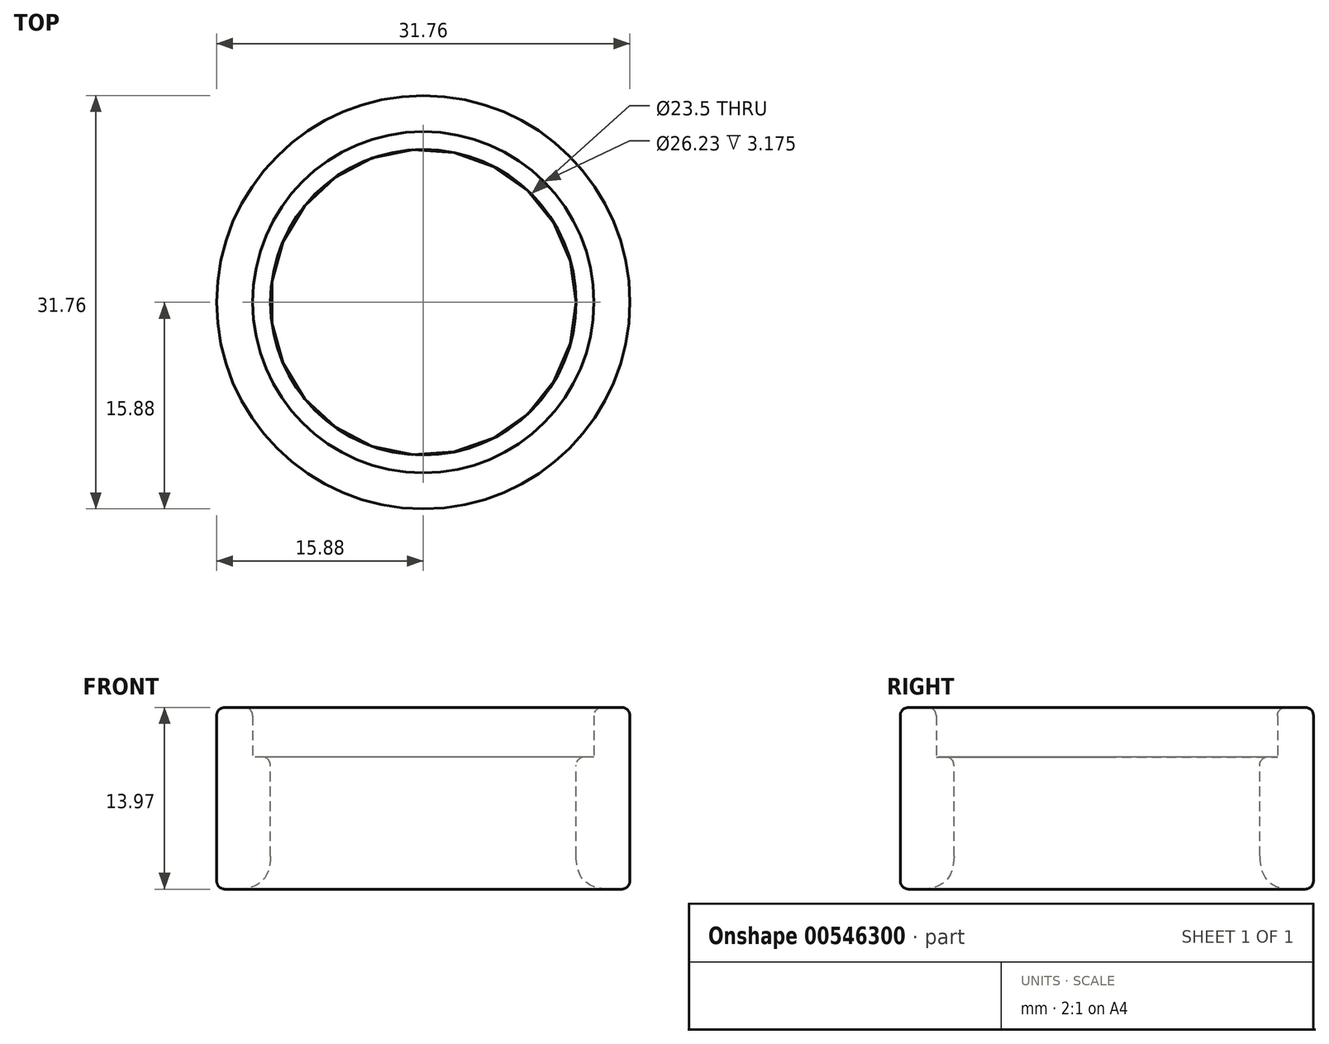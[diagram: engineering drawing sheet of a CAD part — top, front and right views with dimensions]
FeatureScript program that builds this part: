
annotation { "Feature Type Name" : "Feature", "Feature Type Description" : "" }
export const myFeature = defineFeature(function(context is Context, id is Id, definition is map)
    precondition{}
    {
        {
            var Q0;
            Q0=qCreatedBy(makeId("Top.planeOp"),FACE);
            var sketch = newSketch(context, id + "F0", { "sketchPlane" : qUnion([Q0])});
            skCircle(sketch, "E0", {"center": v(0, 0) * mm, "radius": 11.75 * mm});
            skCircle(sketch, "E1", {"center": v(0, 0) * mm, "radius": 13.11 * mm});
            skCircle(sketch, "E2", {"center": v(0, 0) * mm, "radius": 15.88 * mm});
            skSolve(sketch);
        }
        {
            var Q0;
            Q0=makeQuery(id+"F0.imprint","IMPRINT",FACE,{"disambiguationData":[TD([[makeQuery(id+"F0.imprint","IMPRINT",EDGE,{"derivedFrom":sQuery(id+"F0.wireOp",EDGE,"E1")}),-1.0]])]});
            var Q1;
            Q1=makeQuery(id+"F0.imprint","IMPRINT",FACE,{"disambiguationData":[TD([[makeQuery(id+"F0.imprint","IMPRINT",EDGE,{"derivedFrom":sQuery(id+"F0.wireOp",EDGE,"E0")}),-1.0]])]});
            extrude(context, id + "F1", {"entities" : qUnion([Q0, Q1]), "oppositeDirection" : true, "depth" : 10.16 * mm, "offsetDistance" : 25.4 * mm});
        }
        {
            var Q0;
            Q0=makeQuery(id+"F0.imprint","IMPRINT",FACE,{"disambiguationData":[TD([[makeQuery(id+"F0.imprint","IMPRINT",EDGE,{"derivedFrom":sQuery(id+"F0.wireOp",EDGE,"E1")}),-1.0]])]});
            extrude(context, id + "F2", {"entities" : qUnion([Q0]), "operationType" : NewBodyOperationType.ADD, "depth" : 3.8 * mm, "offsetDistance" : 25.4 * mm});
        }
        {
            var Q0;
            Q0=makeQuery(id+"F2.opExtrude","CAP_EDGE",EDGE,{"disambiguationData":[OSD([sQuery(id+"F0.wireOp",EDGE,"E1")])],"isStart":false});
            var Q1;
            Q1=makeQuery(id+"F2.opExtrude","CAP_EDGE",EDGE,{"disambiguationData":[OSD([sQuery(id+"F0.wireOp",EDGE,"E2")])],"isStart":false});
            var Q2;
            Q2=makeQuery(id+"F1.opExtrude","CAP_EDGE",EDGE,{"disambiguationData":[OSD([sQuery(id+"F0.wireOp",EDGE,"E2")])],"isStart":false});
            var Q3;
            Q3=makeQuery(id+"F1.opExtrude","CAP_EDGE",EDGE,{"disambiguationData":[OSD([sQuery(id+"F0.wireOp",EDGE,"E0")])],"isStart":true});
            fillet(context, id + "F3", {"entities" : qUnion([Q0, Q1, Q2, Q3]), "radius" : 0.64 * mm, "tangentPropagation" : true, "allowEdgeOverflow" : false});
        }
        {
            var Q0;
            Q0=makeQuery(id+"F1.opExtrude","CAP_EDGE",EDGE,{"disambiguationData":[OSD([sQuery(id+"F0.wireOp",EDGE,"E0")])],"isStart":false});
            fillet(context, id + "F4", {"entities" : qUnion([Q0]), "radius" : 2.54 * mm, "tangentPropagation" : true, "rho" : 0.5, "crossSection" : FilletCrossSection.CONIC, "allowEdgeOverflow" : false});
        }
    });
